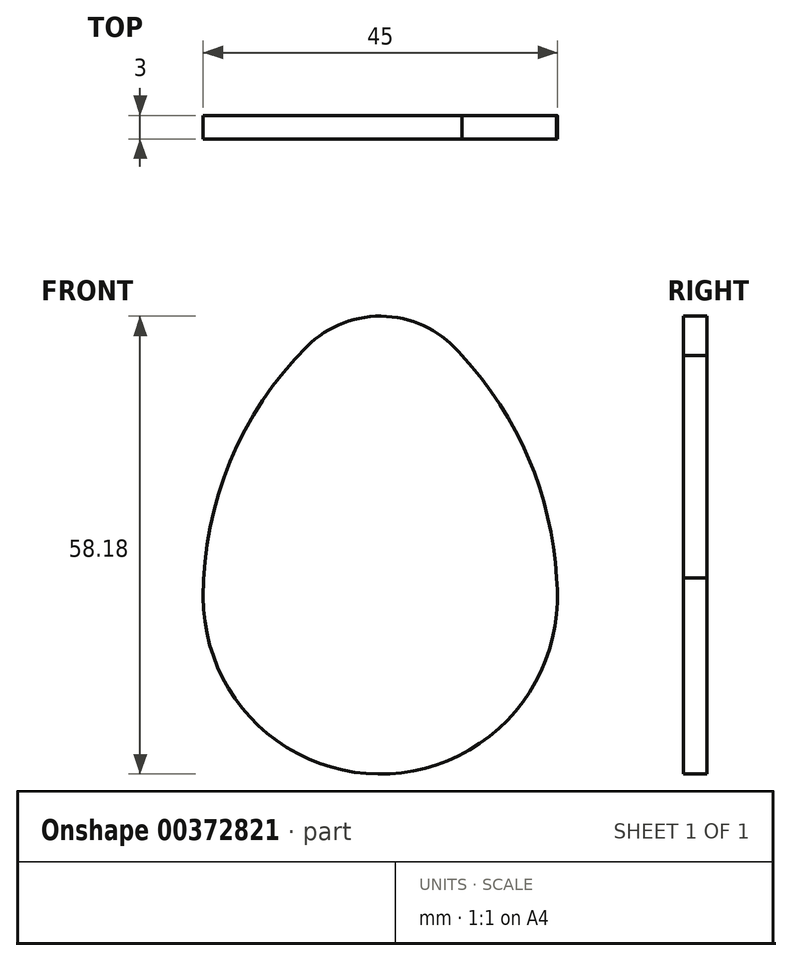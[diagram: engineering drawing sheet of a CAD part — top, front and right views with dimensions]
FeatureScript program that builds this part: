
annotation { "Feature Type Name" : "Feature", "Feature Type Description" : "" }
export const myFeature = defineFeature(function(context is Context, id is Id, definition is map)
    precondition{}
    {
        {
            var Q0;
            Q0=qCreatedBy(makeId("Front.planeOp"),FACE);
            var sketch = newSketch(context, id + "F0", { "sketchPlane" : qUnion([Q0])});
            skArc(sketch, "E0", {"start": v(-22.5, 0) * mm, "mid": v(1.2, -22.47) * mm, "end": v(22.37, 2.42) * mm});
            skArc(sketch, "E1", {"start": v(22.37, -2.42) * mm, "mid": v(19.18, 16.8) * mm, "end": v(8.16, 32.85) * mm});
            skArc(sketch, "E2", {"start": v(-9.32, 31.82) * mm, "mid": v(-19.07, 17.22) * mm, "end": v(-22.5, 0) * mm});
            skArc(sketch, "E3", {"start": v(10.35, 30.66) * mm, "mid": v(0.78, 35.66) * mm, "end": v(-9.32, 31.82) * mm});
            skSolve(sketch);
        }
        {
            var Q0;
            Q0 = qSketchRegion(id + "F0", true);
            extrude(context, id + "F1", {"entities" : qUnion([Q0]), "depth" : 3 * mm});
        }
    });
